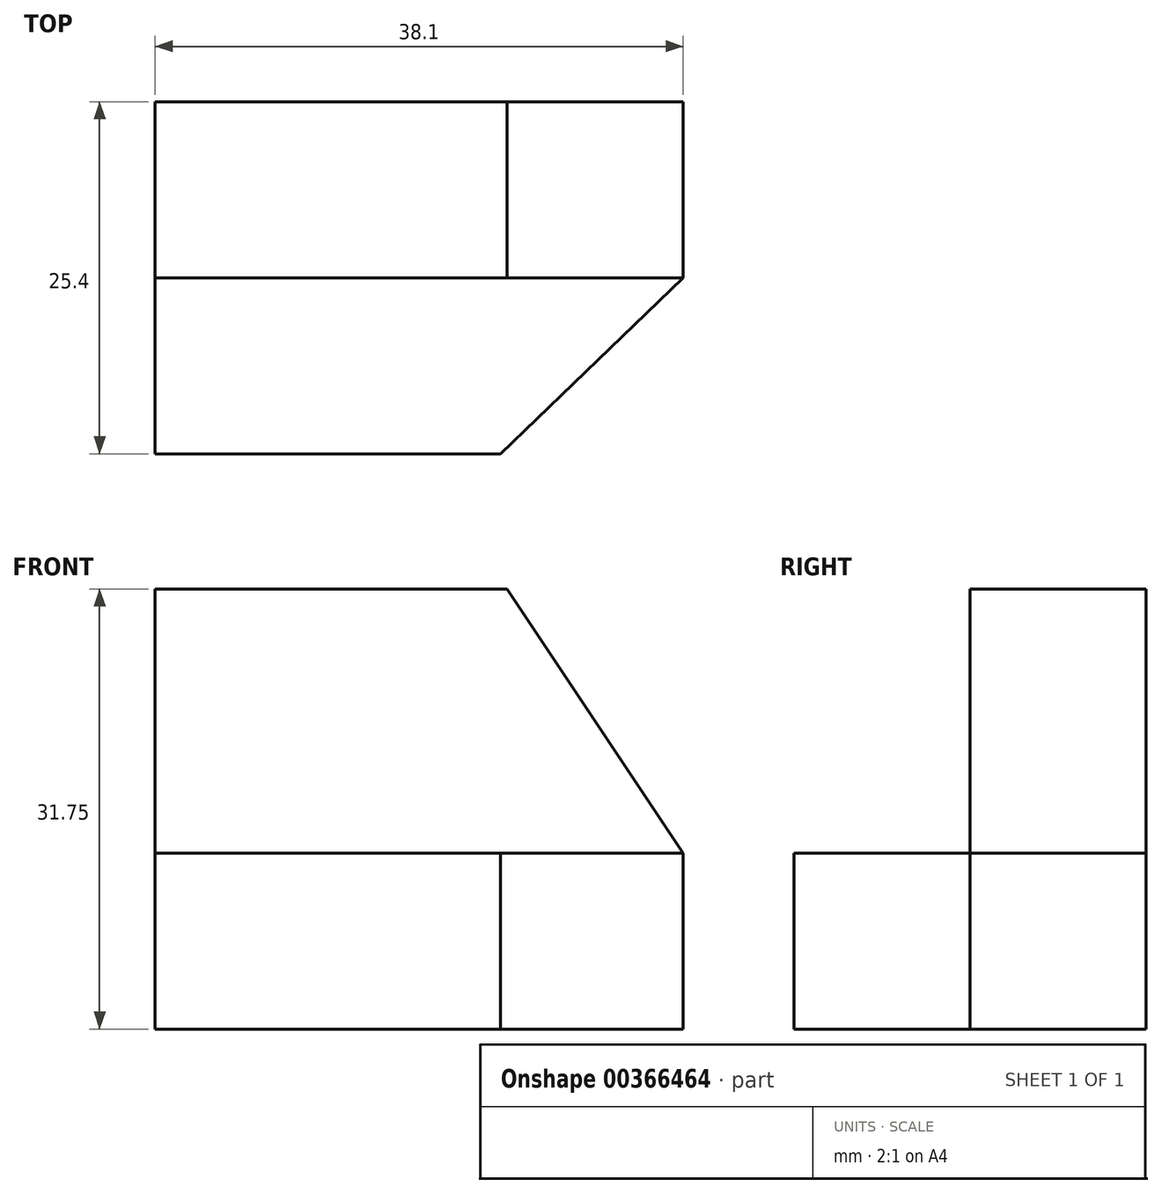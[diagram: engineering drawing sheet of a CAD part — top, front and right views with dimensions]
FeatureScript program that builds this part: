
annotation { "Feature Type Name" : "Feature", "Feature Type Description" : "" }
export const myFeature = defineFeature(function(context is Context, id is Id, definition is map)
    precondition{}
    {
        {
            var Q0;
            Q0=qCreatedBy(makeId("Front.planeOp"),FACE);
            var sketch = newSketch(context, id + "F0", { "sketchPlane" : qUnion([Q0])});
            skLineSegment(sketch, "E0", {"start": v(0, 0) * mm, "end": v(0, 31.75) * mm});
            skLineSegment(sketch, "E1", {"start": v(0, 31.75) * mm, "end": v(25.4, 31.75) * mm});
            skLineSegment(sketch, "E2", {"start": v(25.4, 31.75) * mm, "end": v(38.1, 12.7) * mm});
            skLineSegment(sketch, "E3", {"start": v(38.1, 12.7) * mm, "end": v(38.1, 0) * mm});
            skLineSegment(sketch, "E4", {"start": v(38.1, 0) * mm, "end": v(0, 0) * mm});
            skSolve(sketch);
        }
        {
            var Q0;
            Q0=makeQuery(id+"F0.imprint","IMPRINT",FACE,{"disambiguationData":[TD([[makeQuery(id+"F0.imprint","IMPRINT",EDGE,{"derivedFrom":sQuery(id+"F0.wireOp",EDGE,"E0")}),-1.0]])]});
            extrude(context, id + "F1", {"entities" : qUnion([Q0]), "depth" : 25.4 * mm});
        }
        {
            var Q0;
            Q0=makeQuery(id+"F1.opExtrude","CAP_FACE",FACE,{"disambiguationData":[OSD([sQuery(id+"F0.wireOp",EDGE,"E0"),sQuery(id+"F0.wireOp",EDGE,"E1"),sQuery(id+"F0.wireOp",EDGE,"E2"),sQuery(id+"F0.wireOp",EDGE,"E3"),sQuery(id+"F0.wireOp",EDGE,"E4")])],"isStart":false});
            var sketch = newSketch(context, id + "F2", { "sketchPlane" : qUnion([Q0])});
            skLineSegment(sketch, "E5", {"start": v(0, 12.7) * mm, "end": v(38.1, 12.7) * mm});
            skLineSegment(sketch, "E6", {"start": v(38.1, 12.7) * mm, "end": v(38.1, 0) * mm});
            skLineSegment(sketch, "E7", {"start": v(38.1, 0) * mm, "end": v(0, 0) * mm});
            skLineSegment(sketch, "E8", {"start": v(0, 0) * mm, "end": v(0, 12.7) * mm});
            skSolve(sketch);
        }
        {
            var Q0;
            Q0 = qSketchRegion(id + "F2", true);
            var Q1;
            {var subQ0=sQuery(id+"F2.wireOp",EDGE,"E5");Q1=makeQuery(id+"F2.imprint","IMPRINT",FACE,{"disambiguationData":[TD([[makeQuery(id+"F2.imprint","IMPRINT",EDGE,{"derivedFrom":subQ0}),1.0]])]});}
            extrude(context, id + "F3", {"entities" : qUnion([Q0, Q1]), "operationType" : NewBodyOperationType.REMOVE, "oppositeDirection" : true, "depth" : 12.7 * mm});
        }
        {
            var Q0;
            Q0=makeQuery(id+"F3.boolean.opBoolean","COPY",FACE,{"derivedFrom":makeQuery(id+"F3.opExtrude","CAP_FACE",FACE,{"disambiguationData":[OSD([sQuery(id+"F0.wireOp",EDGE,"E0"),sQuery(id+"F0.wireOp",EDGE,"E1"),sQuery(id+"F0.wireOp",EDGE,"E2"),sQuery(id+"F2.wireOp",EDGE,"E6"),sQuery(id+"F2.wireOp",EDGE,"E7"),sQuery(id+"F2.wireOp",EDGE,"E8")])],"isStart":false})});
            var sketch = newSketch(context, id + "F4", { "sketchPlane" : qUnion([Q0])});
            skLineSegment(sketch, "E9", {"start": v(38.1, 12.7) * mm, "end": v(0, 12.7) * mm});
            skLineSegment(sketch, "E10", {"start": v(0, 12.7) * mm, "end": v(0, 0) * mm});
            skLineSegment(sketch, "E11", {"start": v(0, 0) * mm, "end": v(38.1, 0) * mm});
            skLineSegment(sketch, "E12", {"start": v(38.1, 0) * mm, "end": v(38.1, 12.7) * mm});
            skSolve(sketch);
        }
        {
            var Q0;
            Q0=makeQuery(id+"F4.imprint","IMPRINT",FACE,{"disambiguationData":[TD([[makeQuery(id+"F4.imprint","IMPRINT",EDGE,{"derivedFrom":sQuery(id+"F4.wireOp",EDGE,"E9")}),1.0]])]});
            extrude(context, id + "F5", {"entities" : qUnion([Q0]), "operationType" : NewBodyOperationType.ADD, "depth" : 12.7 * mm});
        }
        {
            var Q0;
            Q0=makeQuery(id+"F5.opExtrude","SWEPT_FACE",FACE,{"disambiguationData":[OSD([sQuery(id+"F4.wireOp",EDGE,"E9")])]});
            var sketch = newSketch(context, id + "F6", { "sketchPlane" : qUnion([Q0])});
            skLineSegment(sketch, "E13", {"start": v(38.1, -12.7) * mm, "end": v(24.93, -25.4) * mm});
            skLineSegment(sketch, "E14", {"start": v(24.93, -25.4) * mm, "end": v(38.1, -25.4) * mm});
            skLineSegment(sketch, "E15", {"start": v(38.1, -25.4) * mm, "end": v(38.1, -12.7) * mm});
            skSolve(sketch);
        }
        {
            var Q0;
            Q0=makeQuery(id+"F6.imprint","IMPRINT",FACE,{"disambiguationData":[TD([[makeQuery(id+"F6.imprint","IMPRINT",EDGE,{"derivedFrom":sQuery(id+"F6.wireOp",EDGE,"E13")}),1.0]])]});
            extrude(context, id + "F7", {"entities" : qUnion([Q0]), "operationType" : NewBodyOperationType.REMOVE, "oppositeDirection" : true, "depth" : 12.7 * mm});
        }
    });
